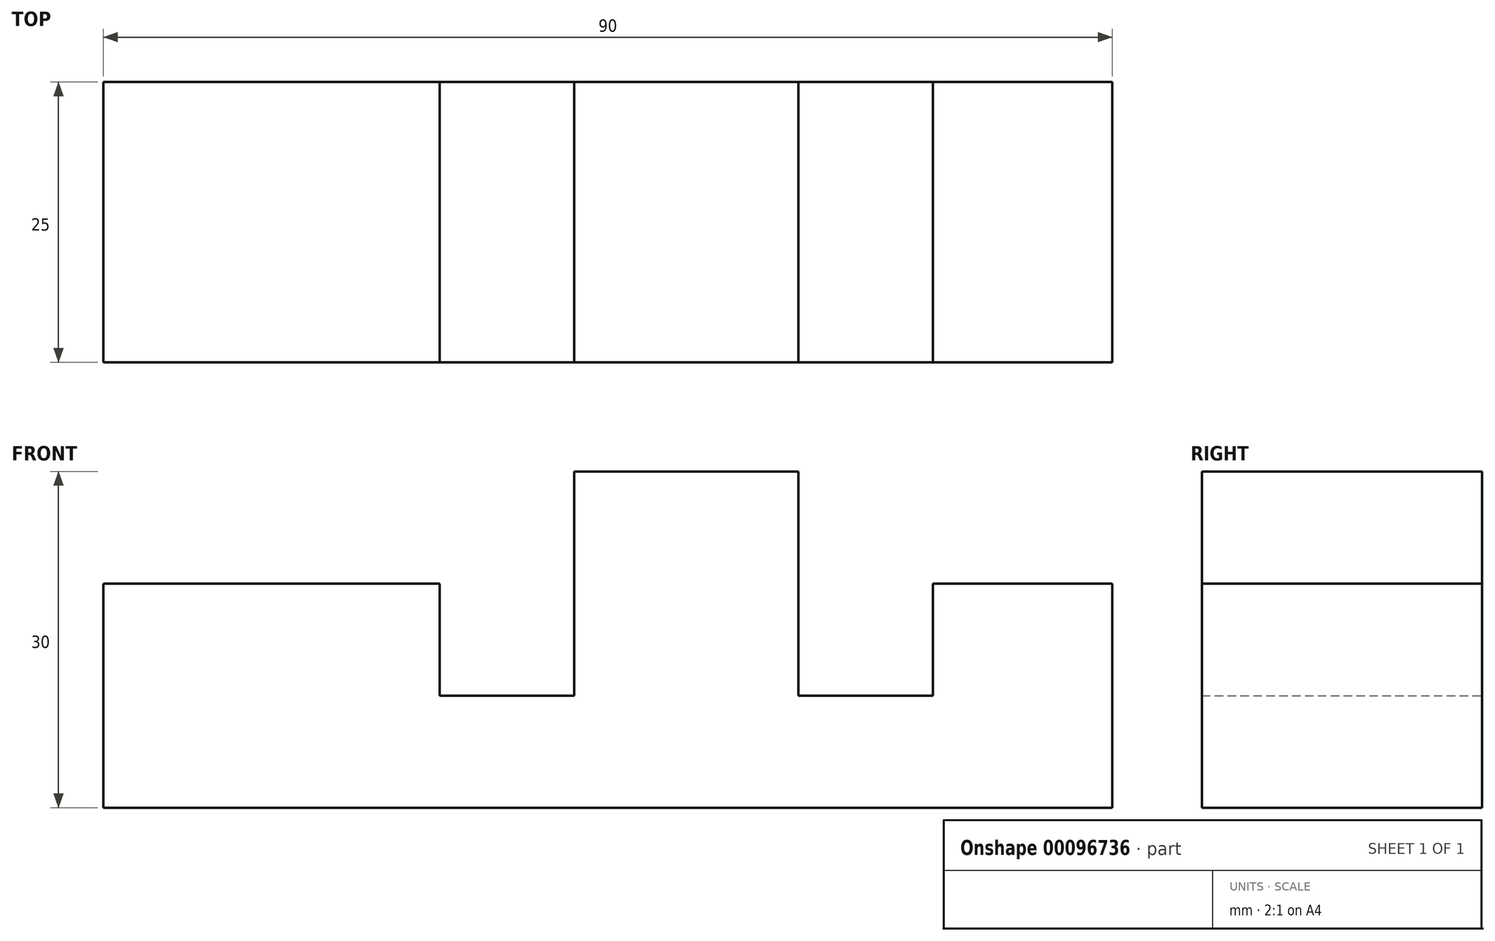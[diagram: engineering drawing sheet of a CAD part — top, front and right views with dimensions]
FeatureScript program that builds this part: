
annotation { "Feature Type Name" : "Feature", "Feature Type Description" : "" }
export const myFeature = defineFeature(function(context is Context, id is Id, definition is map)
    precondition{}
    {
        {
            var Q0;
            Q0=qCreatedBy(makeId("Front.planeOp"),FACE);
            var sketch = newSketch(context, id + "F0", { "sketchPlane" : qUnion([Q0])});
            skLineSegment(sketch, "E0", {"start": v(0, 0) * mm, "end": v(90, 0) * mm});
            skLineSegment(sketch, "E1", {"start": v(90, 0) * mm, "end": v(90, 20) * mm});
            skLineSegment(sketch, "E2", {"start": v(90, 20) * mm, "end": v(74, 20) * mm});
            skLineSegment(sketch, "E3", {"start": v(74, 20) * mm, "end": v(74, 10) * mm});
            skLineSegment(sketch, "E4", {"start": v(74, 10) * mm, "end": v(62, 10) * mm});
            skLineSegment(sketch, "E5", {"start": v(62, 10) * mm, "end": v(62, 30) * mm});
            skLineSegment(sketch, "E6", {"start": v(62, 30) * mm, "end": v(42, 30) * mm});
            skLineSegment(sketch, "E7", {"start": v(42, 30) * mm, "end": v(42, 10) * mm});
            skLineSegment(sketch, "E8", {"start": v(42, 10) * mm, "end": v(30, 10) * mm});
            skLineSegment(sketch, "E9", {"start": v(30, 10) * mm, "end": v(30, 20) * mm});
            skLineSegment(sketch, "E10", {"start": v(30, 20) * mm, "end": v(0, 20) * mm});
            skLineSegment(sketch, "E11", {"start": v(0, 20) * mm, "end": v(0, 0) * mm});
            skLineSegment(sketch, "E12", {"start": v(30, 20) * mm, "end": v(74, 20) * mm, "construction": true});
            skLineSegment(sketch, "E13", {"start": v(42, 10) * mm, "end": v(62, 10) * mm, "construction": true});
            skSolve(sketch);
        }
        {
            var Q0;
            Q0=makeQuery(id+"F0.imprint","IMPRINT",FACE,{"disambiguationData":[TD([[makeQuery(id+"F0.imprint","IMPRINT",EDGE,{"derivedFrom":sQuery(id+"F0.wireOp",EDGE,"E0")}),1.0]])]});
            extrude(context, id + "F1", {"entities" : qUnion([Q0]), "depth" : 25 * mm});
        }
    });
